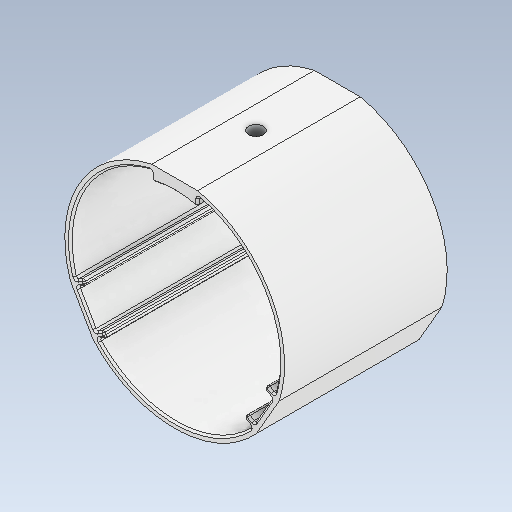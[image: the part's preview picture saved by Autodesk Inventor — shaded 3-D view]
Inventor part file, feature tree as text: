
AUTODESK INVENTOR PART (.ipt)
format: ipt  version: 2020 (Build 240168000, 168)  size: 220,160 bytes
history: native  units: in
note: dims shown in document units (in); Inventor stores cm internally (conversion verified against a paired STEP export)
features: chamfer x1
ambient origin geometry x8: Origin, YZ Plane, XZ Plane, XY Plane, X Axis, Y Axis, Z Axis, Center Point
bodies: Solid1 (feature_tree)
feature tree (1):
  chamfer  "Chamfer1"  [1 undecoded]
note: 1 required parameter value undecoded (feature->parameter linkage not recoverable at this tier; creation-order binding heuristic only, values carry confidence <= 0.55)
